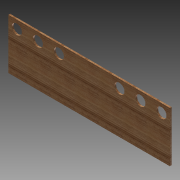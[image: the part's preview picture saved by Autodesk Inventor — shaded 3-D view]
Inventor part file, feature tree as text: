
AUTODESK INVENTOR PART (.ipt)
format: ipt  version: 2012 (Build 160160000, 160)  size: 104,448 bytes
history: native  units: in
note: dims shown in document units (in); Inventor stores cm internally (conversion verified against a paired STEP export)
features: extrude x1, sketch x1
ambient origin geometry x8: Origin, YZ Plane, XZ Plane, XY Plane, X Axis, Y Axis, Z Axis, Center Point
bodies: Solid1 (feature_tree)
feature tree (2):
  extrude  "Extrusion1"  Depth=24.0in
  sketch  "Sketch1"  dims[d0=7.5in d1=24.0in d11=0.25in d12=0.0in d13=1.5in d14=1.5in d15=9.0in d16=6.25in d17=3.125in d18=3.125in d19=1.25in d20=23.5in d21=1.25in d22=1.25in d23=1.25in]
